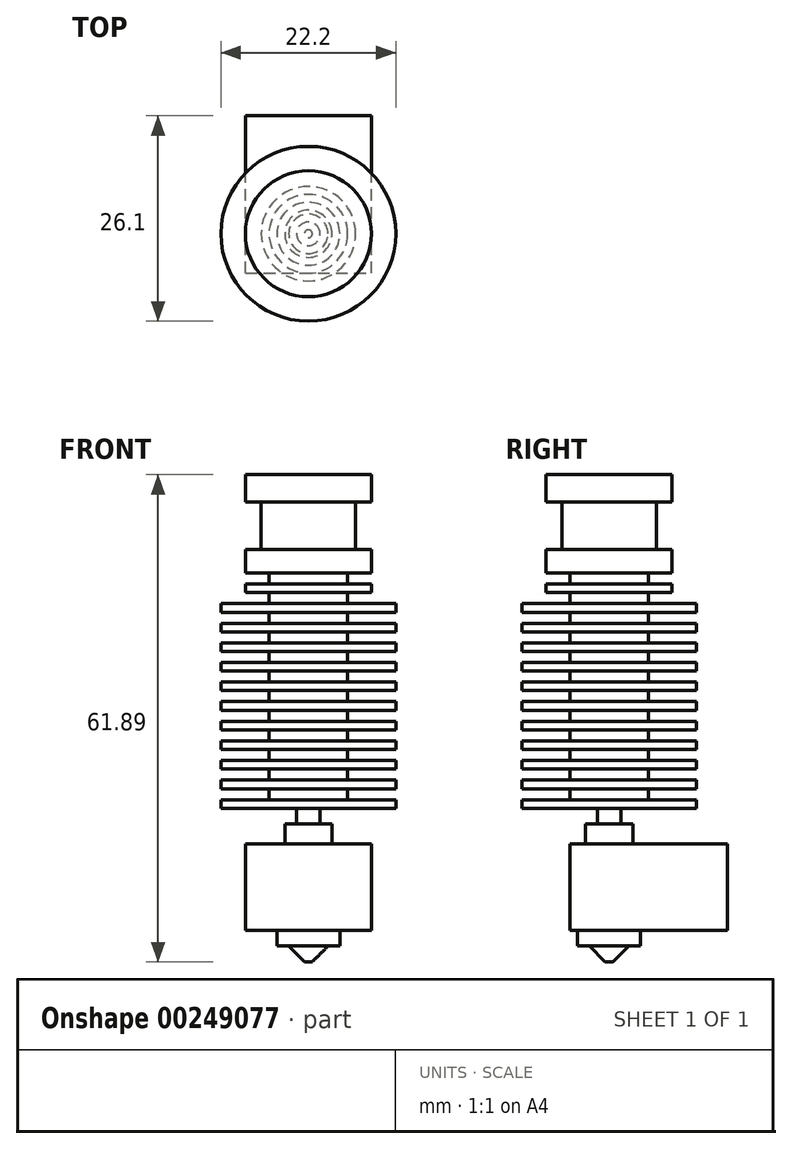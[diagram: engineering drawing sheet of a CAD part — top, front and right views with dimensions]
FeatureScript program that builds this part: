
annotation { "Feature Type Name" : "Feature", "Feature Type Description" : "" }
export const myFeature = defineFeature(function(context is Context, id is Id, definition is map)
    precondition{}
    {
        {
            var Q0;
            Q0=qCreatedBy(makeId("Front.planeOp"),FACE);
            var sketch = newSketch(context, id + "F0", { "sketchPlane" : qUnion([Q0])});
            skLineSegment(sketch, "E0", {"start": v(0, 38.75) * mm, "end": v(0, -39.42) * mm, "construction": true});
            skLineSegment(sketch, "E1", {"start": v(0, 24.95) * mm, "end": v(-8, 24.95) * mm});
            skLineSegment(sketch, "E2", {"start": v(-8, 24.95) * mm, "end": v(-8, 21.45) * mm});
            skLineSegment(sketch, "E3", {"start": v(-8, 21.45) * mm, "end": v(-6, 21.45) * mm});
            skLineSegment(sketch, "E4", {"start": v(-6, 21.45) * mm, "end": v(-6, 15.45) * mm});
            skLineSegment(sketch, "E5", {"start": v(-6, 15.45) * mm, "end": v(-8, 15.45) * mm});
            skLineSegment(sketch, "E6", {"start": v(-8, 15.45) * mm, "end": v(-8, 12.45) * mm});
            skLineSegment(sketch, "E7", {"start": v(-8, 12.45) * mm, "end": v(-5, 12.45) * mm});
            skLineSegment(sketch, "E8", {"start": v(-5, 12.45) * mm, "end": v(-5, 11.05) * mm});
            skLineSegment(sketch, "E9", {"start": v(-5, 11.05) * mm, "end": v(-8, 11.05) * mm});
            skLineSegment(sketch, "E10", {"start": v(-8, 11.05) * mm, "end": v(-8, 9.96) * mm});
            skLineSegment(sketch, "E11", {"start": v(-8, 9.96) * mm, "end": v(-5, 9.96) * mm});
            skLineSegment(sketch, "E12", {"start": v(-5, 9.96) * mm, "end": v(-5, 8.56) * mm});
            skLineSegment(sketch, "E13", {"start": v(-5, 8.56) * mm, "end": v(-11.1, 8.56) * mm});
            skLineSegment(sketch, "E14", {"start": v(-11.1, 8.56) * mm, "end": v(-11.1, 7.47) * mm});
            skLineSegment(sketch, "E15", {"start": v(-11.1, 7.47) * mm, "end": v(-5, 7.47) * mm});
            skLineSegment(sketch, "E16", {"start": v(-5, 7.47) * mm, "end": v(-5, 6.07) * mm});
            skLineSegment(sketch, "E17", {"start": v(-5, 6.07) * mm, "end": v(-11.1, 6.07) * mm});
            skLineSegment(sketch, "E18", {"start": v(-11.1, 6.07) * mm, "end": v(-11.1, 4.98) * mm});
            skLineSegment(sketch, "E19", {"start": v(-11.1, 4.98) * mm, "end": v(-5, 4.98) * mm});
            skLineSegment(sketch, "E20", {"start": v(-5, 4.98) * mm, "end": v(-5, 3.58) * mm});
            skLineSegment(sketch, "E21", {"start": v(-5, 3.58) * mm, "end": v(-11.1, 3.58) * mm});
            skLineSegment(sketch, "E22", {"start": v(-11.1, 3.58) * mm, "end": v(-11.1, 2.5) * mm});
            skLineSegment(sketch, "E23", {"start": v(-11.1, 2.5) * mm, "end": v(-5, 2.5) * mm});
            skLineSegment(sketch, "E24", {"start": v(-5, 2.5) * mm, "end": v(-5, 1.1) * mm});
            skLineSegment(sketch, "E25", {"start": v(-5, 1.1) * mm, "end": v(-11.1, 1.1) * mm});
            skLineSegment(sketch, "E26", {"start": v(-11.1, 1.1) * mm, "end": v(-11.1, 0) * mm});
            skLineSegment(sketch, "E27", {"start": v(-11.1, 0) * mm, "end": v(-5, 0) * mm});
            skLineSegment(sketch, "E28", {"start": v(-5, 0) * mm, "end": v(-5, -1.4) * mm});
            skLineSegment(sketch, "E29", {"start": v(-5, -1.4) * mm, "end": v(-11.1, -1.4) * mm});
            skLineSegment(sketch, "E30", {"start": v(-11.1, -1.4) * mm, "end": v(-11.1, -2.5) * mm});
            skLineSegment(sketch, "E31", {"start": v(-11.1, -2.5) * mm, "end": v(-5, -2.5) * mm});
            skLineSegment(sketch, "E32", {"start": v(-5, -2.5) * mm, "end": v(-5, -3.9) * mm});
            skLineSegment(sketch, "E33", {"start": v(-5, -3.9) * mm, "end": v(-11.1, -3.9) * mm});
            skLineSegment(sketch, "E34", {"start": v(-11.1, -3.9) * mm, "end": v(-11.1, -4.98) * mm});
            skLineSegment(sketch, "E35", {"start": v(-11.1, -4.98) * mm, "end": v(-5, -4.98) * mm});
            skLineSegment(sketch, "E36", {"start": v(-5, -4.98) * mm, "end": v(-5, -6.38) * mm});
            skLineSegment(sketch, "E37", {"start": v(-5, -6.38) * mm, "end": v(-11.1, -6.38) * mm});
            skLineSegment(sketch, "E38", {"start": v(-11.1, -6.38) * mm, "end": v(-11.1, -7.47) * mm});
            skLineSegment(sketch, "E39", {"start": v(-11.1, -7.47) * mm, "end": v(-5, -7.47) * mm});
            skLineSegment(sketch, "E40", {"start": v(-5, -7.47) * mm, "end": v(-5, -8.87) * mm});
            skLineSegment(sketch, "E41", {"start": v(-5, -8.87) * mm, "end": v(-11.1, -8.87) * mm});
            skLineSegment(sketch, "E42", {"start": v(-11.1, -8.87) * mm, "end": v(-11.1, -9.96) * mm});
            skLineSegment(sketch, "E43", {"start": v(-11.1, -9.96) * mm, "end": v(-5, -9.96) * mm});
            skLineSegment(sketch, "E44", {"start": v(-5, -9.96) * mm, "end": v(-5, -11.36) * mm});
            skLineSegment(sketch, "E45", {"start": v(-5, -11.36) * mm, "end": v(-11.1, -11.36) * mm});
            skLineSegment(sketch, "E46", {"start": v(-11.1, -11.36) * mm, "end": v(-11.1, -12.45) * mm});
            skLineSegment(sketch, "E47", {"start": v(-11.1, -12.45) * mm, "end": v(-5, -12.45) * mm});
            skLineSegment(sketch, "E48", {"start": v(-5, -12.45) * mm, "end": v(-5, -13.85) * mm});
            skLineSegment(sketch, "E49", {"start": v(-5, -13.85) * mm, "end": v(-11.1, -13.85) * mm});
            skLineSegment(sketch, "E50", {"start": v(-11.1, -13.85) * mm, "end": v(-11.1, -14.95) * mm});
            skLineSegment(sketch, "E51", {"start": v(-11.1, -14.95) * mm, "end": v(-5, -14.95) * mm});
            skLineSegment(sketch, "E52", {"start": v(-5, -14.95) * mm, "end": v(-5, -16.35) * mm});
            skLineSegment(sketch, "E53", {"start": v(-5, -16.35) * mm, "end": v(-11.1, -16.35) * mm});
            skLineSegment(sketch, "E54", {"start": v(-11.1, -16.35) * mm, "end": v(-11.1, -17.44) * mm});
            skLineSegment(sketch, "E55", {"start": v(-11.1, -17.44) * mm, "end": v(0, -17.44) * mm});
            skLineSegment(sketch, "E56", {"start": v(-1.5, -17.44) * mm, "end": v(-1.5, -19.44) * mm});
            skLineSegment(sketch, "E57", {"start": v(-1.5, -19.44) * mm, "end": v(-3, -19.44) * mm});
            skLineSegment(sketch, "E58", {"start": v(-3, -19.44) * mm, "end": v(-3, -32.94) * mm});
            skLineSegment(sketch, "E59", {"start": v(-3, -32.94) * mm, "end": v(-4, -32.94) * mm});
            skLineSegment(sketch, "E60", {"start": v(-4, -32.94) * mm, "end": v(-4, -34.94) * mm});
            skLineSegment(sketch, "E61", {"start": v(-4, -34.94) * mm, "end": v(-2.5, -34.94) * mm});
            skLineSegment(sketch, "E62", {"start": v(-2.5, -34.94) * mm, "end": v(-0.5, -36.94) * mm});
            skLineSegment(sketch, "E63", {"start": v(-0.5, -36.94) * mm, "end": v(0, -36.94) * mm});
            skLineSegment(sketch, "E64", {"start": v(0, -36.94) * mm, "end": v(0, -17.44) * mm});
            skLineSegment(sketch, "E65", {"start": v(0, 24.95) * mm, "end": v(0, -17.44) * mm});
            skSolve(sketch);
        }
        {
            var Q0;
            {var subQ0=sQuery(id+"F0.wireOp",EDGE,"E56");Q0=makeQuery(id+"F0.imprint","IMPRINT",FACE,{"disambiguationData":[TD([[makeQuery(id+"F0.imprint","IMPRINT",EDGE,{"derivedFrom":subQ0}),1.0]])]});}
            var Q1;
            Q1=makeQuery(id+"F0.imprint","IMPRINT",FACE,{"disambiguationData":[TD([[makeQuery(id+"F0.imprint","IMPRINT",EDGE,{"derivedFrom":sQuery(id+"F0.wireOp",EDGE,"E1")}),1.0]])]});
            var Q2;
            Q2=sQuery(id+"F0.wireOp",EDGE,"E0");
            revolve(context, id + "F1", {"entities" : qUnion([Q0, Q1]), "axis" : qUnion([Q2]), "revolveType" : RevolveType.FULL});
        }
        {
            var Q0;
            Q0=qCreatedBy(makeId("Front.planeOp"),FACE);
            var sketch = newSketch(context, id + "F2", { "sketchPlane" : qUnion([Q0])});
            skLineSegment(sketch, "E66.0", {"start": v(-3, -19.44) * mm, "end": v(-3, -32.94) * mm, "construction": true});
            skLineSegment(sketch, "E66.1", {"start": v(-1.5, -19.44) * mm, "end": v(-3, -19.44) * mm, "construction": true});
            skLineSegment(sketch, "E66.2", {"start": v(0, -36.94) * mm, "end": v(0, -17.44) * mm, "construction": true});
            skLineSegment(sketch, "E67.bottom", {"start": v(-8, -21.94) * mm, "end": v(8, -21.94) * mm});
            skLineSegment(sketch, "E67.top", {"start": v(-8, -32.94) * mm, "end": v(8, -32.94) * mm});
            skLineSegment(sketch, "E67.left", {"start": v(-8, -21.94) * mm, "end": v(-8, -32.94) * mm});
            skLineSegment(sketch, "E67.right", {"start": v(8, -21.94) * mm, "end": v(8, -32.94) * mm});
            skPoint(sketch, "E68", {"position": v(0, -21.94) * mm});
            skLineSegment(sketch, "E69.0", {"start": v(-3, -32.94) * mm, "end": v(3, -32.94) * mm, "construction": true});
            skSolve(sketch);
        }
        {
            var Q0;
            Q0 = qSketchRegion(id + "F2", true);
            extrude(context, id + "F3", {"entities" : qUnion([Q0]), "operationType" : NewBodyOperationType.ADD, "depth" : 5 * mm, "hasSecondDirection" : true, "secondDirectionOppositeDirection" : true, "secondDirectionDepth" : 15 * mm});
        }
    });
